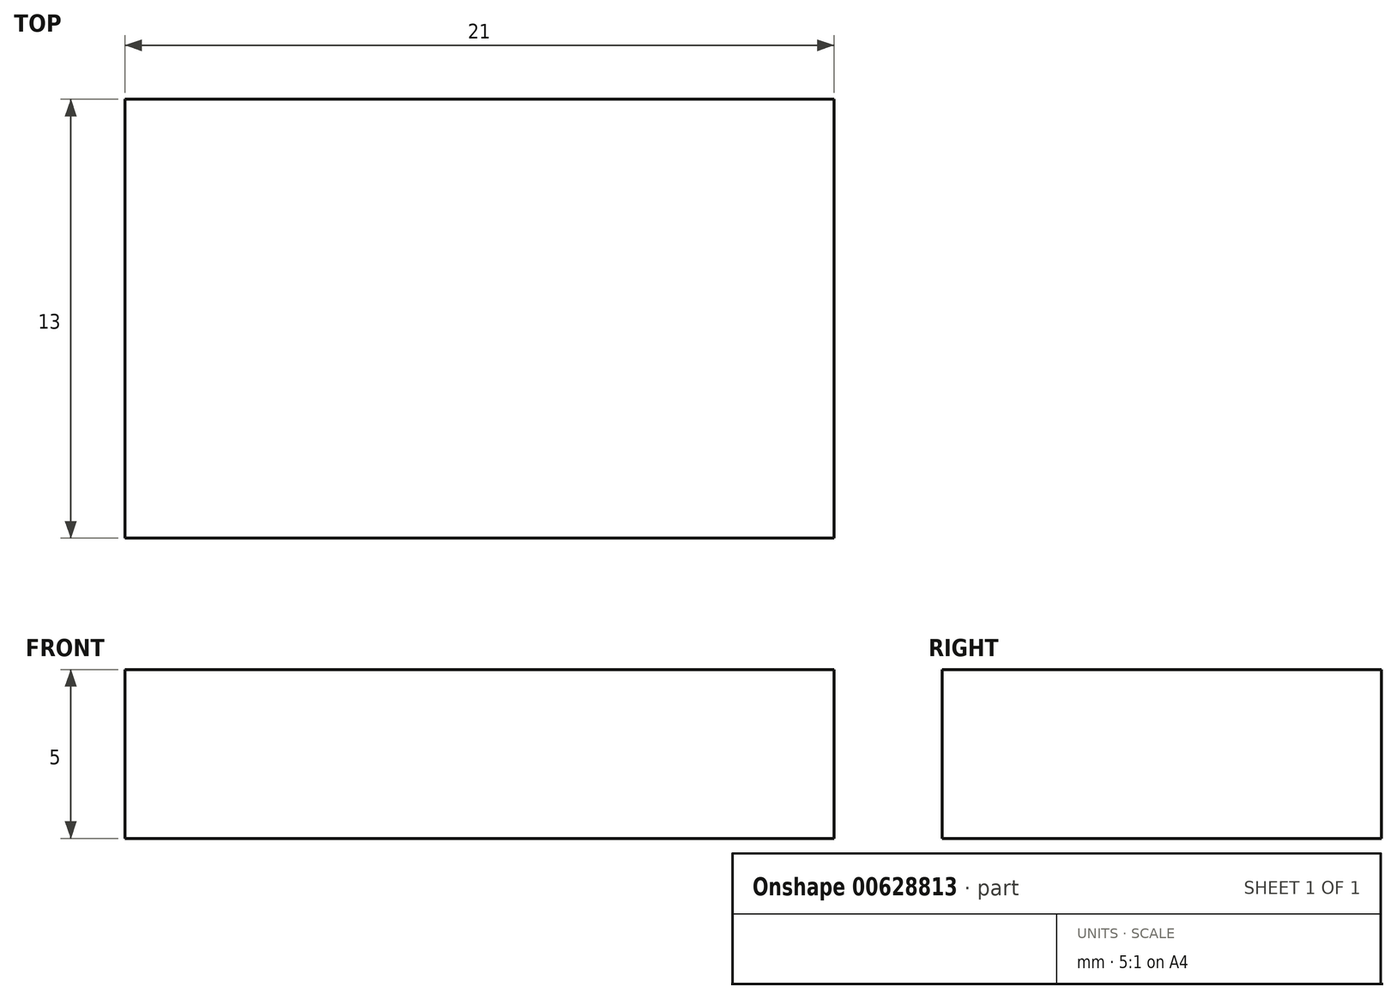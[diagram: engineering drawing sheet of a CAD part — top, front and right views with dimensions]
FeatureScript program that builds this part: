
annotation { "Feature Type Name" : "Feature", "Feature Type Description" : "" }
export const myFeature = defineFeature(function(context is Context, id is Id, definition is map)
    precondition{}
    {
        {
            var Q0;
            Q0=qCreatedBy(makeId("Top.planeOp"),FACE);
            var sketch = newSketch(context, id + "F0", { "sketchPlane" : qUnion([Q0])});
            skLineSegment(sketch, "E0.bottom", {"start": v(10.5, 6.5) * mm, "end": v(-10.5, 6.5) * mm});
            skLineSegment(sketch, "E0.top", {"start": v(10.5, -6.5) * mm, "end": v(-10.5, -6.5) * mm});
            skLineSegment(sketch, "E0.left", {"start": v(10.5, 6.5) * mm, "end": v(10.5, -6.5) * mm});
            skLineSegment(sketch, "E0.right", {"start": v(-10.5, 6.5) * mm, "end": v(-10.5, -6.5) * mm});
            skPoint(sketch, "E0.middle", {"position": v(0, 0) * mm});
            skSolve(sketch);
        }
        {
            var Q0;
            Q0 = qSketchRegion(id + "F0", true);
            extrude(context, id + "F1", {"entities" : qUnion([Q0]), "depth" : 5 * mm, "offsetDistance" : 25 * mm, "symmetric" : true});
        }
    });
